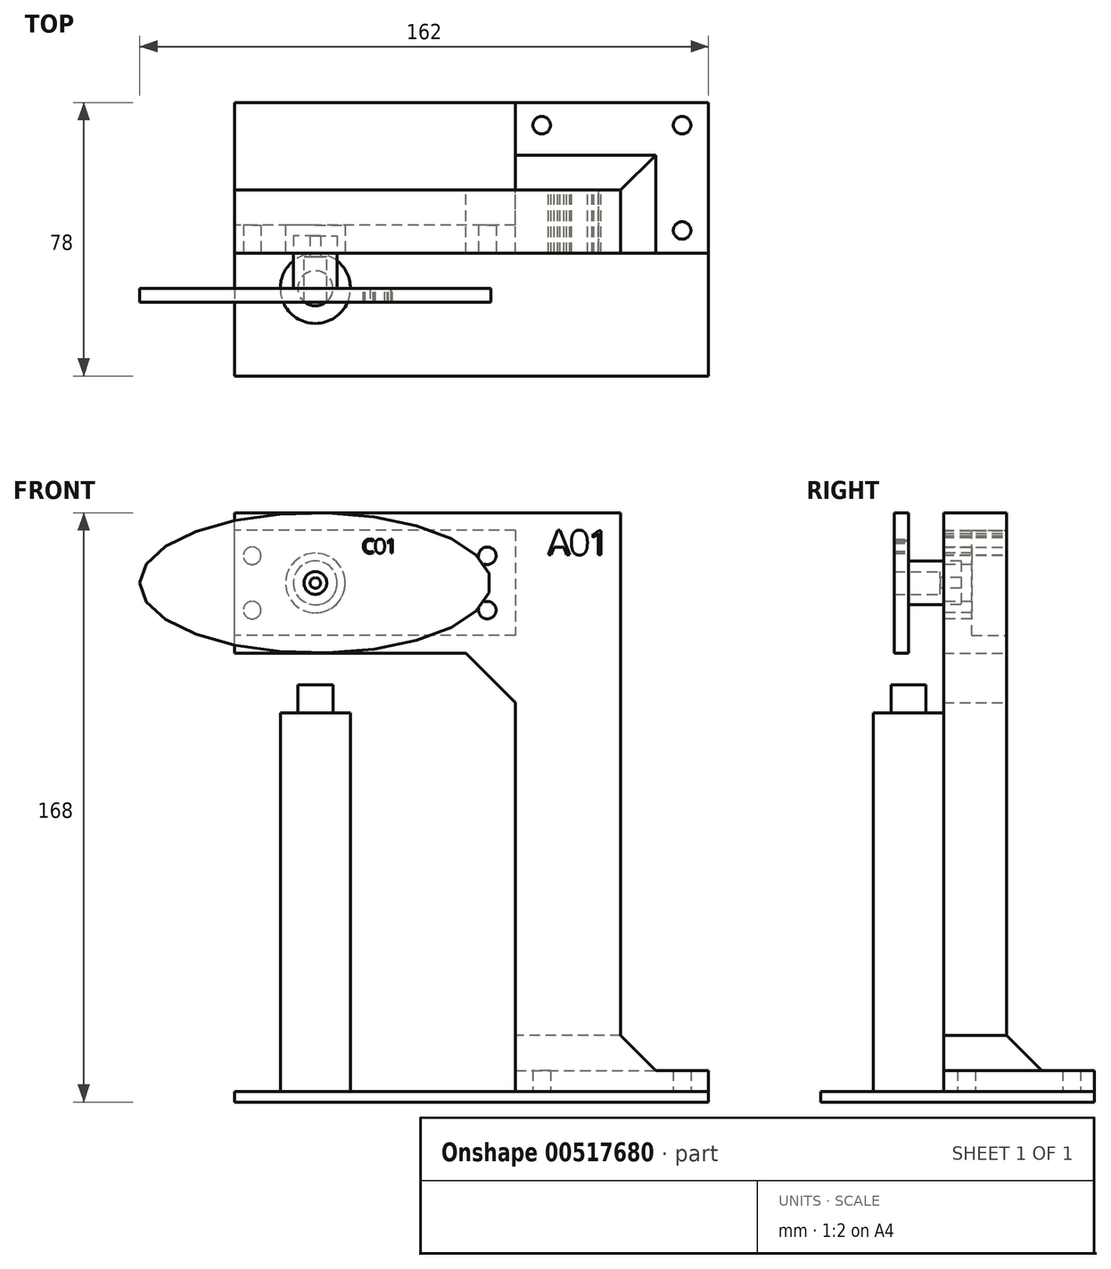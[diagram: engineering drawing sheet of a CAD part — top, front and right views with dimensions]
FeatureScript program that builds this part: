
annotation { "Feature Type Name" : "Feature", "Feature Type Description" : "" }
export const myFeature = defineFeature(function(context is Context, id is Id, definition is map)
    precondition{}
    {
        {
            var Q0;
            Q0=qCreatedBy(makeId("Front.planeOp"),FACE);
            var sketch = newSketch(context, id + "F0", { "sketchPlane" : qUnion([Q0])});
            skLineSegment(sketch, "E0", {"start": v(0, 0) * mm, "end": v(0, 110.86) * mm});
            skLineSegment(sketch, "E1", {"start": v(0, 110.86) * mm, "end": v(-14.14, 125) * mm});
            skLineSegment(sketch, "E2", {"start": v(-14.14, 125) * mm, "end": v(-80, 125) * mm});
            skLineSegment(sketch, "E3", {"start": v(-80, 125) * mm, "end": v(-80, 165) * mm});
            skLineSegment(sketch, "E4", {"start": v(-80, 165) * mm, "end": v(30, 165) * mm});
            skLineSegment(sketch, "E5", {"start": v(30, 165) * mm, "end": v(30, 0) * mm});
            skLineSegment(sketch, "E6", {"start": v(30, 0) * mm, "end": v(0, 0) * mm});
            skLineSegment(sketch, "E7", {"start": v(-14.14, 125) * mm, "end": v(0, 125) * mm, "construction": true});
            skLineSegment(sketch, "E8", {"start": v(0, 125) * mm, "end": v(0, 110.86) * mm, "construction": true});
            skText(sketch, "E9", { "text": "A01", "fontName": "OpenSans-Regular.ttf"});
            skLineSegment(sketch, "E10", {"start": v(25, 165) * mm, "end": v(25, 160) * mm, "construction": true});
            skLineSegment(sketch, "E11", {"start": v(25, 160) * mm, "end": v(30, 160) * mm, "construction": true});
            const initialGuessF0  = {"E9": [0.00934, 0.15303, 1, 0, 0.00697]};
            skSetInitialGuess(sketch, initialGuessF0);
            skSolve(sketch);
        }
        {
            var Q0;
            Q0=qSketchRegion(id+"F0",true);
            extrude(context, id + "F1", {"entities" : qUnion([Q0]), "depth" : 18 * mm, "offsetDistance" : 25 * mm});
        }
        {
            var Q0;
            Q0=makeQuery(id+"F1.opExtrude","CAP_FACE",FACE,{"disambiguationData":[OSD([sQuery(id+"F0.wireOp",EDGE,"E0"),sQuery(id+"F0.wireOp",EDGE,"E1"),sQuery(id+"F0.wireOp",EDGE,"E2"),sQuery(id+"F0.wireOp",EDGE,"E3"),sQuery(id+"F0.wireOp",EDGE,"E4"),sQuery(id+"F0.wireOp",EDGE,"E5"),sQuery(id+"F0.wireOp",EDGE,"E6")])],"isStart":false});
            var sketch = newSketch(context, id + "F2", { "sketchPlane" : qUnion([Q0])});
            skCircle(sketch, "E12", {"center": v(-75, 152.75) * mm, "radius": 2.5 * mm});
            skCircle(sketch, "E13", {"center": v(-75, 137.25) * mm, "radius": 2.5 * mm});
            skCircle(sketch, "E14", {"center": v(-8, 137.25) * mm, "radius": 2.5 * mm});
            skCircle(sketch, "E15", {"center": v(-8, 152.75) * mm, "radius": 2.5 * mm});
            skCircle(sketch, "E16", {"center": v(-57, 145) * mm, "radius": 8.5 * mm});
            skLineSegment(sketch, "E17", {"start": v(-75, 152.75) * mm, "end": v(-57, 152.75) * mm, "construction": true});
            skLineSegment(sketch, "E18", {"start": v(-57, 152.75) * mm, "end": v(-57, 145) * mm, "construction": true});
            skLineSegment(sketch, "E19", {"start": v(-75, 137.25) * mm, "end": v(-57, 137.25) * mm, "construction": true});
            skLineSegment(sketch, "E20", {"start": v(-57, 137.25) * mm, "end": v(-57, 145) * mm, "construction": true});
            skSolve(sketch);
        }
        {
            var Q0;
            Q0=qSketchRegion(id+"F2",true);
            extrude(context, id + "F3", {"entities" : qUnion([Q0]), "operationType" : NewBodyOperationType.REMOVE, "endBound" : BoundingType.THROUGH_ALL, "oppositeDirection" : true, "depth" : 25 * mm, "offsetDistance" : 25 * mm});
        }
        {
            var Q0;
            Q0=makeQuery(id+"F1.opExtrude","CAP_FACE",FACE,{"disambiguationData":[OSD([sQuery(id+"F0.wireOp",EDGE,"E0"),sQuery(id+"F0.wireOp",EDGE,"E1"),sQuery(id+"F0.wireOp",EDGE,"E2"),sQuery(id+"F0.wireOp",EDGE,"E3"),sQuery(id+"F0.wireOp",EDGE,"E4"),sQuery(id+"F0.wireOp",EDGE,"E5"),sQuery(id+"F0.wireOp",EDGE,"E6")])],"isStart":true});
            var sketch = newSketch(context, id + "F4", { "sketchPlane" : qUnion([Q0])});
            skLineSegment(sketch, "E21.bottom", {"start": v(0, 160) * mm, "end": v(80, 160) * mm});
            skLineSegment(sketch, "E21.top", {"start": v(0, 130) * mm, "end": v(80, 130) * mm});
            skLineSegment(sketch, "E21.left", {"start": v(0, 160) * mm, "end": v(0, 130) * mm});
            skLineSegment(sketch, "E21.right", {"start": v(80, 160) * mm, "end": v(80, 130) * mm});
            skSolve(sketch);
        }
        {
            var Q0;
            Q0=qSketchRegion(id+"F4",true);
            extrude(context, id + "F5", {"entities" : qUnion([Q0]), "operationType" : NewBodyOperationType.REMOVE, "oppositeDirection" : true, "depth" : 10 * mm, "offsetDistance" : 25 * mm});
        }
        {
            var Q0;
            Q0=qCreatedBy(makeId("Top.planeOp"),FACE);
            var sketch = newSketch(context, id + "F6", { "sketchPlane" : qUnion([Q0])});
            skLineSegment(sketch, "E22.top", {"start": v(0, 25) * mm, "end": v(55, 25) * mm});
            skLineSegment(sketch, "E22.right", {"start": v(55, -18) * mm, "end": v(55, 25) * mm});
            skCircle(sketch, "E23", {"center": v(7.5, 18.5) * mm, "radius": 2.5 * mm});
            skCircle(sketch, "E24", {"center": v(47.5, 18.5) * mm, "radius": 2.5 * mm});
            skCircle(sketch, "E25", {"center": v(47.5, -11.5) * mm, "radius": 2.5 * mm});
            skLineSegment(sketch, "E26", {"start": v(0, -18) * mm, "end": v(30, -18) * mm});
            skLineSegment(sketch, "E27", {"start": v(30, -18) * mm, "end": v(55, -18) * mm});
            skLineSegment(sketch, "E28", {"start": v(0, -18) * mm, "end": v(0, 0) * mm});
            skLineSegment(sketch, "E29", {"start": v(0, 0) * mm, "end": v(0, 25) * mm});
            skLineSegment(sketch, "E30", {"start": v(0, 18.5) * mm, "end": v(7.5, 18.5) * mm, "construction": true});
            skLineSegment(sketch, "E31", {"start": v(47.5, 18.5) * mm, "end": v(55, 18.5) * mm, "construction": true});
            skLineSegment(sketch, "E32", {"start": v(47.5, -11.5) * mm, "end": v(47.5, -18) * mm, "construction": true});
            skLineSegment(sketch, "E33", {"start": v(47.5, 18.5) * mm, "end": v(47.5, 25) * mm, "construction": true});
            skSolve(sketch);
        }
        {
            var Q0;
            Q0=qSketchRegion(id+"F6",true);
            extrude(context, id + "F7", {"entities" : qUnion([Q0]), "operationType" : NewBodyOperationType.ADD, "depth" : 6 * mm, "offsetDistance" : 25 * mm});
        }
        {
            var Q0;
            Q0=makeQuery(id+"F7.boolean.opBoolean","INTERSECT",EDGE,{"derivedFrom":[makeQuery(id+"F1.opExtrude","SWEPT_FACE",FACE,{"disambiguationData":[OSD([sQuery(id+"F0.wireOp",EDGE,"E5")])]}),makeQuery(id+"F7.opExtrude","CAP_FACE",FACE,{"disambiguationData":[OSD([sQuery(id+"F6.wireOp",EDGE,"E22.top"),sQuery(id+"F6.wireOp",EDGE,"E22.right"),sQuery(id+"F6.wireOp",EDGE,"E23"),sQuery(id+"F6.wireOp",EDGE,"E24"),sQuery(id+"F6.wireOp",EDGE,"E25"),sQuery(id+"F6.wireOp",EDGE,"E26"),sQuery(id+"F6.wireOp",EDGE,"E27"),sQuery(id+"F6.wireOp",EDGE,"E28"),sQuery(id+"F6.wireOp",EDGE,"E29")])],"isStart":false})]});
            var Q1;
            Q1=makeQuery(id+"F7.boolean.opBoolean","INTERSECT",EDGE,{"derivedFrom":[makeQuery(id+"F1.opExtrude","CAP_FACE",FACE,{"disambiguationData":[OSD([sQuery(id+"F0.wireOp",EDGE,"E0"),sQuery(id+"F0.wireOp",EDGE,"E1"),sQuery(id+"F0.wireOp",EDGE,"E2"),sQuery(id+"F0.wireOp",EDGE,"E3"),sQuery(id+"F0.wireOp",EDGE,"E4"),sQuery(id+"F0.wireOp",EDGE,"E5"),sQuery(id+"F0.wireOp",EDGE,"E6"),sQuery(id+"F0.wireOp",EDGE,"E9.sketch_text.stroke-0"),sQuery(id+"F0.wireOp",EDGE,"E9.sketch_text.stroke-1"),sQuery(id+"F0.wireOp",EDGE,"E9.sketch_text.stroke-2"),sQuery(id+"F0.wireOp",EDGE,"E9.sketch_text.stroke-3"),sQuery(id+"F0.wireOp",EDGE,"E9.sketch_text.stroke-4"),sQuery(id+"F0.wireOp",EDGE,"E9.sketch_text.stroke-5"),sQuery(id+"F0.wireOp",EDGE,"E9.sketch_text.stroke-6"),sQuery(id+"F0.wireOp",EDGE,"E9.sketch_text.stroke-7"),sQuery(id+"F0.wireOp",EDGE,"E9.sketch_text.stroke-13"),sQuery(id+"F0.wireOp",EDGE,"E9.sketch_text.stroke-14"),sQuery(id+"F0.wireOp",EDGE,"E9.sketch_text.stroke-15"),sQuery(id+"F0.wireOp",EDGE,"E9.sketch_text.stroke-16"),sQuery(id+"F0.wireOp",EDGE,"E9.sketch_text.stroke-17"),sQuery(id+"F0.wireOp",EDGE,"E9.sketch_text.stroke-18"),sQuery(id+"F0.wireOp",EDGE,"E9.sketch_text.stroke-19"),sQuery(id+"F0.wireOp",EDGE,"E9.sketch_text.stroke-20"),sQuery(id+"F0.wireOp",EDGE,"E9.sketch_text.stroke-29"),sQuery(id+"F0.wireOp",EDGE,"E9.sketch_text.stroke-30"),sQuery(id+"F0.wireOp",EDGE,"E9.sketch_text.stroke-31"),sQuery(id+"F0.wireOp",EDGE,"E9.sketch_text.stroke-32"),sQuery(id+"F0.wireOp",EDGE,"E9.sketch_text.stroke-33"),sQuery(id+"F0.wireOp",EDGE,"E9.sketch_text.stroke-34"),sQuery(id+"F0.wireOp",EDGE,"E9.sketch_text.stroke-35"),sQuery(id+"F0.wireOp",EDGE,"E9.sketch_text.stroke-36"),sQuery(id+"F0.wireOp",EDGE,"E9.sketch_text.stroke-37")])],"isStart":true}),makeQuery(id+"F7.opExtrude","CAP_FACE",FACE,{"disambiguationData":[OSD([sQuery(id+"F6.wireOp",EDGE,"E22.top"),sQuery(id+"F6.wireOp",EDGE,"E22.right"),sQuery(id+"F6.wireOp",EDGE,"E23"),sQuery(id+"F6.wireOp",EDGE,"E24"),sQuery(id+"F6.wireOp",EDGE,"E25"),sQuery(id+"F6.wireOp",EDGE,"E26"),sQuery(id+"F6.wireOp",EDGE,"E27"),sQuery(id+"F6.wireOp",EDGE,"E28"),sQuery(id+"F6.wireOp",EDGE,"E29")])],"isStart":false})]});
            chamfer(context, id + "F8", {"entities" : qUnion([Q0, Q1]), "width" : 10 * mm, "tangentPropagation" : true});
        }
        {
            var Q0;
            Q0=makeQuery(id+"F1.opExtrude","CAP_FACE",FACE,{"disambiguationData":[OSD([sQuery(id+"F0.wireOp",EDGE,"E0"),sQuery(id+"F0.wireOp",EDGE,"E1"),sQuery(id+"F0.wireOp",EDGE,"E2"),sQuery(id+"F0.wireOp",EDGE,"E3"),sQuery(id+"F0.wireOp",EDGE,"E4"),sQuery(id+"F0.wireOp",EDGE,"E5"),sQuery(id+"F0.wireOp",EDGE,"E6")])],"isStart":false});
            cPlane(context, id + "F9", {"entities" : qUnion([Q0]), "cplaneType" : CPlaneType.OFFSET, "offset" : 10 * mm, "width" : 150 * mm, "height" : 150 * mm});
        }
        {
            var Q0;
            Q0=qCreatedBy(id+"F9.planeOp",FACE);
            var sketch = newSketch(context, id + "F10", { "sketchPlane" : qUnion([Q0])});
            skEllipse(sketch, "E34", {"center": v(-57, 145) * mm, "majorRadius": 50 * mm, "minorRadius": 20 * mm, "majorAxis": v(-1, 0)});
            skCircle(sketch, "E35", {"center": v(-57, 145) * mm, "radius": 3.25 * mm});
            skText(sketch, "E36", { "text": "C01", "fontName": "OpenSans-Regular.ttf"});
            skLineSegment(sketch, "E37", {"start": v(-57, 145) * mm, "end": v(-7, 145) * mm, "construction": true});
            const initialGuessF10  = {"E36": [-0.04367, 0.1535, 1, 0, 0.004]};
            skSetInitialGuess(sketch, initialGuessF10);
            skSolve(sketch);
        }
        {
            var Q0;
            Q0=qSketchRegion(id+"F10",true);
            extrude(context, id + "F11", {"entities" : qUnion([Q0]), "depth" : 4 * mm, "offsetDistance" : 25 * mm});
        }
        {
            var Q0;
            Q0=makeQuery(id+"F11.opExtrude","CAP_FACE",FACE,{"disambiguationData":[OSD([sQuery(id+"F10.wireOp",EDGE,"E34"),sQuery(id+"F10.wireOp",EDGE,"E35"),sQuery(id+"F10.wireOp",EDGE,"E36.sketch_text.stroke-0"),sQuery(id+"F10.wireOp",EDGE,"E36.sketch_text.stroke-1"),sQuery(id+"F10.wireOp",EDGE,"E36.sketch_text.stroke-2"),sQuery(id+"F10.wireOp",EDGE,"E36.sketch_text.stroke-3"),sQuery(id+"F10.wireOp",EDGE,"E36.sketch_text.stroke-4"),sQuery(id+"F10.wireOp",EDGE,"E36.sketch_text.stroke-5"),sQuery(id+"F10.wireOp",EDGE,"E36.sketch_text.stroke-6"),sQuery(id+"F10.wireOp",EDGE,"E36.sketch_text.stroke-7"),sQuery(id+"F10.wireOp",EDGE,"E36.sketch_text.stroke-8"),sQuery(id+"F10.wireOp",EDGE,"E36.sketch_text.stroke-9"),sQuery(id+"F10.wireOp",EDGE,"E36.sketch_text.stroke-10"),sQuery(id+"F10.wireOp",EDGE,"E36.sketch_text.stroke-11"),sQuery(id+"F10.wireOp",EDGE,"E36.sketch_text.stroke-12"),sQuery(id+"F10.wireOp",EDGE,"E36.sketch_text.stroke-13"),sQuery(id+"F10.wireOp",EDGE,"E36.sketch_text.stroke-14"),sQuery(id+"F10.wireOp",EDGE,"E36.sketch_text.stroke-15"),sQuery(id+"F10.wireOp",EDGE,"E36.sketch_text.stroke-16"),sQuery(id+"F10.wireOp",EDGE,"E36.sketch_text.stroke-17"),sQuery(id+"F10.wireOp",EDGE,"E36.sketch_text.stroke-18"),sQuery(id+"F10.wireOp",EDGE,"E36.sketch_text.stroke-19"),sQuery(id+"F10.wireOp",EDGE,"E36.sketch_text.stroke-20"),sQuery(id+"F10.wireOp",EDGE,"E36.sketch_text.stroke-21"),sQuery(id+"F10.wireOp",EDGE,"E36.sketch_text.stroke-22"),sQuery(id+"F10.wireOp",EDGE,"E36.sketch_text.stroke-31"),sQuery(id+"F10.wireOp",EDGE,"E36.sketch_text.stroke-32"),sQuery(id+"F10.wireOp",EDGE,"E36.sketch_text.stroke-33"),sQuery(id+"F10.wireOp",EDGE,"E36.sketch_text.stroke-34"),sQuery(id+"F10.wireOp",EDGE,"E36.sketch_text.stroke-35"),sQuery(id+"F10.wireOp",EDGE,"E36.sketch_text.stroke-36"),sQuery(id+"F10.wireOp",EDGE,"E36.sketch_text.stroke-37"),sQuery(id+"F10.wireOp",EDGE,"E36.sketch_text.stroke-38"),sQuery(id+"F10.wireOp",EDGE,"E36.sketch_text.stroke-39")])],"isStart":true});
            var sketch = newSketch(context, id + "F12", { "sketchPlane" : qUnion([Q0])});
            skCircle(sketch, "E38", {"center": v(57, 145) * mm, "radius": 3.25 * mm});
            skCircle(sketch, "E39", {"center": v(57, 145) * mm, "radius": 6.25 * mm});
            skSolve(sketch);
        }
        {
            var Q0;
            Q0 = qSketchRegion(id + "F12", true);
            extrude(context, id + "F13", {"entities" : qUnion([Q0]), "operationType" : NewBodyOperationType.ADD, "depth" : 9 * mm, "offsetDistance" : 25 * mm});
        }
        {
            var Q0;
            Q0=makeQuery(id+"F13.opExtrude","CAP_FACE",FACE,{"disambiguationData":[OSD([sQuery(id+"F12.wireOp",EDGE,"E38"),sQuery(id+"F12.wireOp",EDGE,"E39")])],"isStart":false});
            var sketch = newSketch(context, id + "F14", { "sketchPlane" : qUnion([Q0])});
            skCircle(sketch, "E40", {"center": v(57, 145) * mm, "radius": 6.25 * mm});
            skCircle(sketch, "E41", {"center": v(57, 145) * mm, "radius": 1.5 * mm});
            skSolve(sketch);
        }
        {
            var Q0;
            Q0 = qSketchRegion(id + "F14", true);
            extrude(context, id + "F15", {"entities" : qUnion([Q0]), "operationType" : NewBodyOperationType.ADD, "depth" : 6 * mm, "offsetDistance" : 25 * mm});
        }
        {
            var Q0;
            Q0=qCreatedBy(id+"F9.planeOp",FACE);
            var sketch = newSketch(context, id + "F16", { "sketchPlane" : qUnion([Q0])});
            skLineSegment(sketch, "E42.bottom", {"start": v(-57, 116) * mm, "end": v(-52, 116) * mm});
            skLineSegment(sketch, "E42.top", {"start": v(-57, 0) * mm, "end": v(-52, 0) * mm});
            skLineSegment(sketch, "E42.left", {"start": v(-57, 116) * mm, "end": v(-57, 0) * mm});
            skLineSegment(sketch, "E42.right", {"start": v(-52, 116) * mm, "end": v(-52, 0) * mm});
            skLineSegment(sketch, "E43.bottom", {"start": v(-52, 108) * mm, "end": v(-47, 108) * mm});
            skLineSegment(sketch, "E43.top", {"start": v(-52, 0) * mm, "end": v(-47, 0) * mm});
            skLineSegment(sketch, "E43.left", {"start": v(-52, 108) * mm, "end": v(-52, 0) * mm});
            skLineSegment(sketch, "E43.right", {"start": v(-47, 108) * mm, "end": v(-47, 0) * mm});
            skLineSegment(sketch, "E44", {"start": v(-57, 145) * mm, "end": v(-57, 116) * mm, "construction": true});
            skSolve(sketch);
        }
        {
            var Q0;
            Q0 = qSketchRegion(id + "F16", true);
            var Q1;
            Q1=sQuery(id+"F16.wireOp",EDGE,"E42.left");
            revolve(context, id + "F17", {"entities" : qUnion([Q0]), "axis" : qUnion([Q1]), "revolveType" : RevolveType.FULL});
        }
        {
            var Q0;
            Q0=qCreatedBy(makeId("Top.planeOp"),FACE);
            var sketch = newSketch(context, id + "F18", { "sketchPlane" : qUnion([Q0])});
            skLineSegment(sketch, "E45.bottom", {"start": v(55, 25) * mm, "end": v(-80, 25) * mm});
            skLineSegment(sketch, "E45.top", {"start": v(55, -53) * mm, "end": v(-80, -53) * mm});
            skLineSegment(sketch, "E45.left", {"start": v(55, 25) * mm, "end": v(55, -53) * mm});
            skLineSegment(sketch, "E45.right", {"start": v(-80, 25) * mm, "end": v(-80, -53) * mm});
            skSolve(sketch);
        }
        {
            var Q0;
            Q0 = qSketchRegion(id + "F18", true);
            extrude(context, id + "F19", {"entities" : qUnion([Q0]), "oppositeDirection" : true, "depth" : 3 * mm, "offsetDistance" : 25 * mm});
        }
    });
